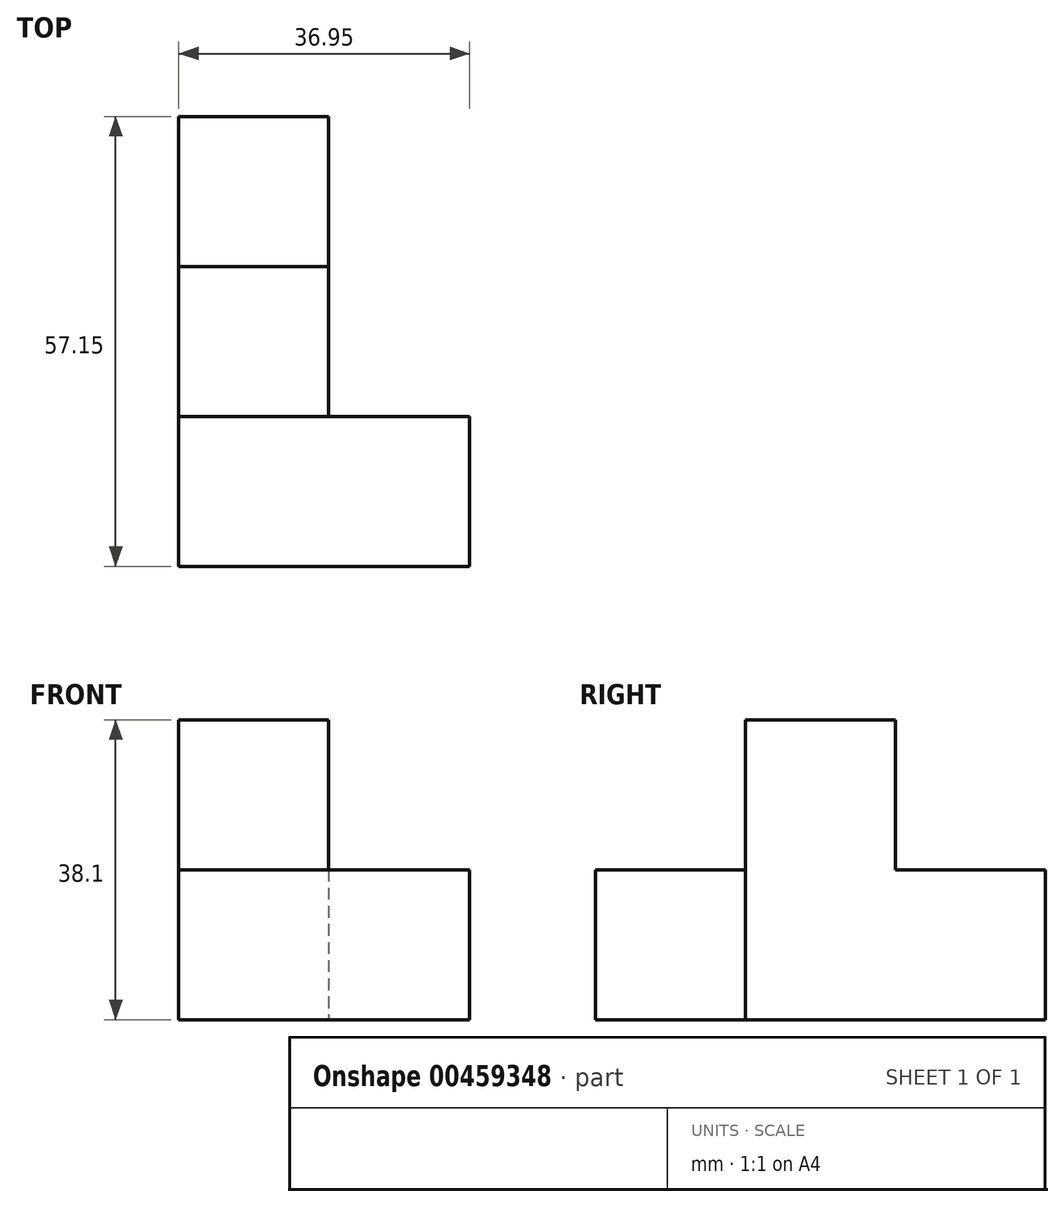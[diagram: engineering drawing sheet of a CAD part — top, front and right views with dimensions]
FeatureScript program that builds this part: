
annotation { "Feature Type Name" : "Feature", "Feature Type Description" : "" }
export const myFeature = defineFeature(function(context is Context, id is Id, definition is map)
    precondition{}
    {
        {
            var Q0;
            Q0=qCreatedBy(makeId("Top.planeOp"),FACE);
            var sketch = newSketch(context, id + "F0", { "sketchPlane" : qUnion([Q0])});
            skLineSegment(sketch, "E0", {"start": v(0, 0) * mm, "end": v(-19.05, 0) * mm});
            skLineSegment(sketch, "E1", {"start": v(-19.05, 0) * mm, "end": v(-19.05, -57.15) * mm});
            skLineSegment(sketch, "E2", {"start": v(-19.05, -57.15) * mm, "end": v(17.9, -57.15) * mm});
            skLineSegment(sketch, "E3", {"start": v(17.9, -57.15) * mm, "end": v(17.9, -38.1) * mm});
            skLineSegment(sketch, "E4", {"start": v(17.9, -38.1) * mm, "end": v(0, -38.1) * mm});
            skLineSegment(sketch, "E5", {"start": v(0, -38.1) * mm, "end": v(0, 0) * mm});
            skLineSegment(sketch, "E6", {"start": v(0, -19.05) * mm, "end": v(-19.05, -19.05) * mm});
            skLineSegment(sketch, "E7", {"start": v(-19.05, -19.05) * mm, "end": v(-19.05, -38.1) * mm});
            skLineSegment(sketch, "E8", {"start": v(-19.05, -38.1) * mm, "end": v(0, -38.1) * mm});
            skSolve(sketch);
        }
        {
            var Q0;
            {var subQ0=sQuery(id+"F0.wireOp",EDGE,"E2");Q0=makeQuery(id+"F0.imprint","IMPRINT",FACE,{"disambiguationData":[TD([[makeQuery(id+"F0.imprint","IMPRINT",EDGE,{"derivedFrom":subQ0}),1.0]])]});}
            extrude(context, id + "F1", {"entities" : qUnion([Q0]), "depth" : 19.05 * mm});
        }
        {
            var Q0;
            {var subQ2=sQuery(id+"F0.wireOp",EDGE,"E6");Q0=makeQuery(id+"F0.imprint","IMPRINT",FACE,{"disambiguationData":[TD([[makeQuery(id+"F0.imprint","IMPRINT",EDGE,{"derivedFrom":subQ2}),1.0]])]});}
            extrude(context, id + "F2", {"entities" : qUnion([Q0]), "operationType" : NewBodyOperationType.ADD, "depth" : 38.1 * mm});
        }
        {
            var Q0;
            {var subQ0=sQuery(id+"F0.wireOp",EDGE,"E0");Q0=makeQuery(id+"F0.imprint","IMPRINT",FACE,{"disambiguationData":[TD([[makeQuery(id+"F0.imprint","IMPRINT",EDGE,{"derivedFrom":subQ0}),1.0]])]});}
            extrude(context, id + "F3", {"entities" : qUnion([Q0]), "operationType" : NewBodyOperationType.ADD, "depth" : 19.05 * mm});
        }
    });
